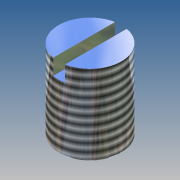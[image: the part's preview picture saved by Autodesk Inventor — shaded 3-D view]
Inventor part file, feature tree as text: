
AUTODESK INVENTOR PART (.ipt)
format: ipt  version: 2014 (Build 180170000, 170)  size: 129,536 bytes
history: native  units: mm (DEFAULTED — no unit token found)
features: extrude x2, sketch x2, chamfer x1, thread x1
ambient origin geometry x8: Origin, YZ Plane, XZ Plane, XY Plane, X Axis, Y Axis, Z Axis, Center Point
bodies: Solid1 (feature_tree)
feature tree (6):
  extrude  "Extrusion1"  Depth=10.3mm TaperAngle=0.0deg
  chamfer  "Chamfer1"  Distance=0.3mm
  thread  "Thread1"  [1 undecoded]
  extrude  "Extrusion2"  Depth=2.0mm
  sketch  "Sketch1"  dims[d0=8.0mm d1=10.3mm d2=0.0mm d3=0.3mm d4=0.3mm d5=10.0mm d6=0.0mm]
  sketch  "Sketch2"  dims[d7=1.5mm d8=0.75mm d9=2.0mm d10=0.0mm d11=45.0deg]
note: 1 required parameter value undecoded (feature->parameter linkage not recoverable at this tier; creation-order binding heuristic only, values carry confidence <= 0.55)
